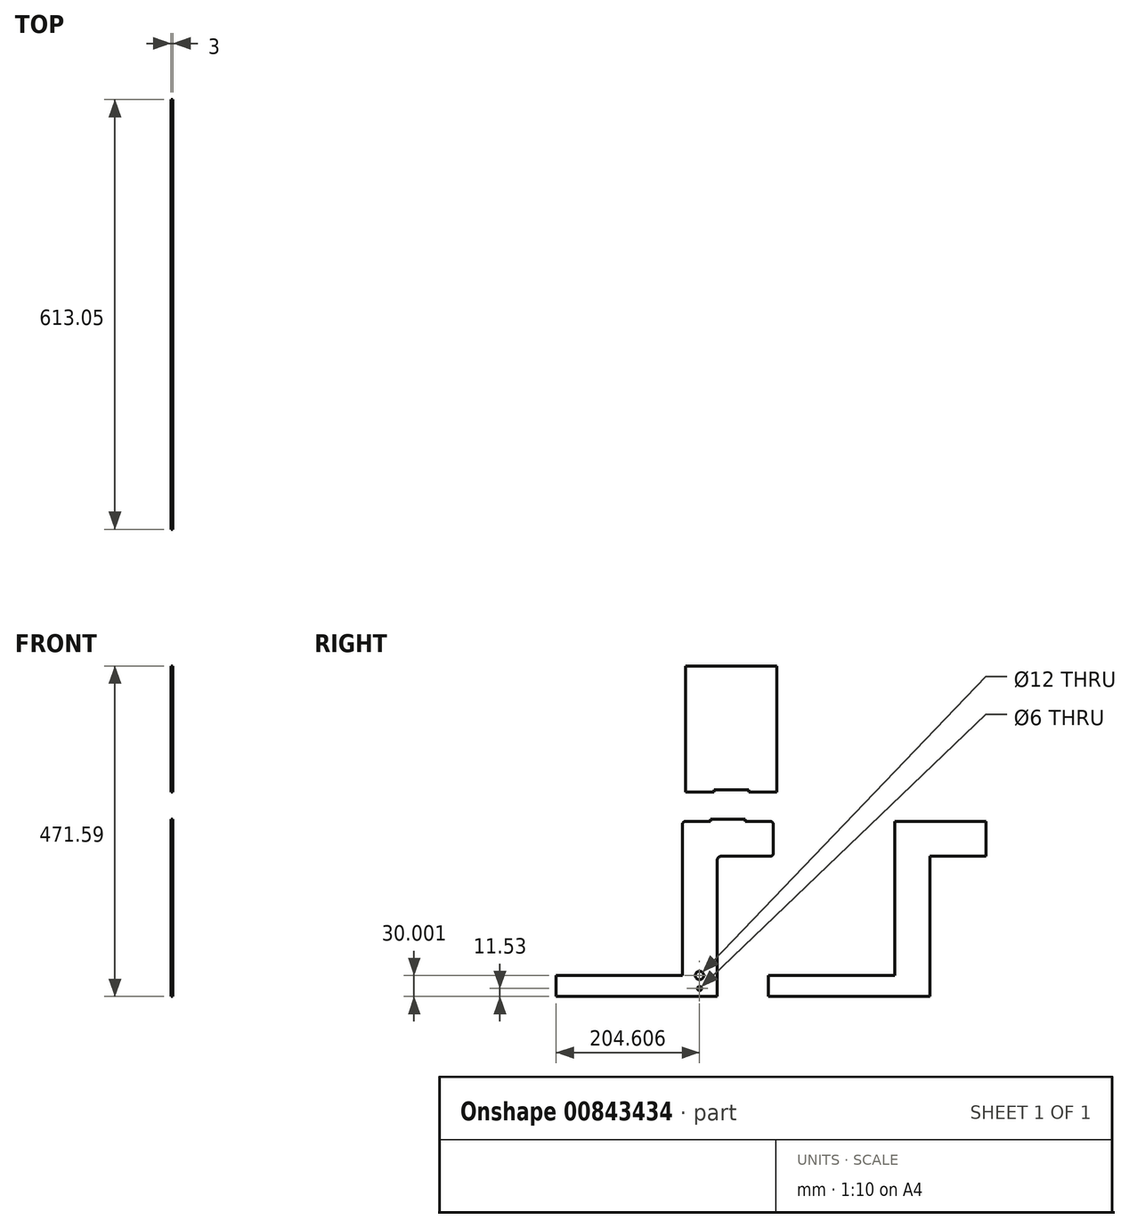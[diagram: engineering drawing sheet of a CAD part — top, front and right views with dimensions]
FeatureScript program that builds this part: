
annotation { "Feature Type Name" : "Feature", "Feature Type Description" : "" }
export const myFeature = defineFeature(function(context is Context, id is Id, definition is map)
    precondition{}
    {
        {
            var Q0;
            Q0=qCreatedBy(makeId("Right.planeOp"),FACE);
            var sketch = newSketch(context, id + "F0", { "sketchPlane" : qUnion([Q0])});
            skLineSegment(sketch, "E0", {"start": v(0, 42.16) * mm, "end": v(130, 42.16) * mm});
            skLineSegment(sketch, "E1", {"start": v(130, 42.16) * mm, "end": v(130, -7.84) * mm});
            skLineSegment(sketch, "E2", {"start": v(50, -7.84) * mm, "end": v(130, -7.84) * mm});
            skLineSegment(sketch, "E3", {"start": v(50, -7.84) * mm, "end": v(50, -207.84) * mm});
            skLineSegment(sketch, "E4", {"start": v(50, -207.84) * mm, "end": v(-180, -207.84) * mm});
            skLineSegment(sketch, "E5", {"start": v(-180, -207.84) * mm, "end": v(-180, -177.84) * mm});
            skLineSegment(sketch, "E6", {"start": v(0, -177.84) * mm, "end": v(-180, -177.84) * mm});
            skLineSegment(sketch, "E7", {"start": v(0, -177.84) * mm, "end": v(0, 42.16) * mm});
            skLineSegment(sketch, "E8", {"start": v(-298.05, 42.16) * mm, "end": v(-263.05, 42.16) * mm});
            skLineSegment(sketch, "E9", {"start": v(-173.05, 37.16) * mm, "end": v(-173.05, -2.84) * mm});
            skLineSegment(sketch, "E10", {"start": v(-248.05, -7.84) * mm, "end": v(-178.05, -7.84) * mm});
            skLineSegment(sketch, "E11", {"start": v(-253.05, -12.84) * mm, "end": v(-253.05, -207.84) * mm});
            skLineSegment(sketch, "E12", {"start": v(-253.05, -207.84) * mm, "end": v(-483.05, -207.84) * mm});
            skLineSegment(sketch, "E13", {"start": v(-483.05, -207.84) * mm, "end": v(-483.05, -177.84) * mm});
            skLineSegment(sketch, "E14", {"start": v(-303.05, -177.84) * mm, "end": v(-483.05, -177.84) * mm});
            skLineSegment(sketch, "E15", {"start": v(-303.05, -177.84) * mm, "end": v(-303.05, 37.16) * mm});
            skCircle(sketch, "E16", {"center": v(-278.44, -177.84) * mm, "radius": 6 * mm});
            skLineSegment(sketch, "E17.bottom", {"start": v(-298.36, 83.75) * mm, "end": v(-258.01, 83.75) * mm});
            skLineSegment(sketch, "E17.top", {"start": v(-298.36, 263.75) * mm, "end": v(-168.36, 263.75) * mm});
            skLineSegment(sketch, "E17.left", {"start": v(-298.36, 83.75) * mm, "end": v(-298.36, 263.75) * mm});
            skLineSegment(sketch, "E17.right", {"start": v(-168.36, 83.75) * mm, "end": v(-168.36, 263.75) * mm});
            skCircle(sketch, "E18", {"center": v(-278.44, -196.31) * mm, "radius": 3 * mm});
            skLineSegment(sketch, "E19", {"start": v(-263.05, 42.16) * mm, "end": v(-263.05, 45.16) * mm});
            skLineSegment(sketch, "E20", {"start": v(-263.05, 45.16) * mm, "end": v(-213.05, 45.16) * mm});
            skLineSegment(sketch, "E21", {"start": v(-213.05, 45.16) * mm, "end": v(-213.05, 42.16) * mm});
            skLineSegment(sketch, "E22.trimOffspring", {"start": v(-213.05, 42.16) * mm, "end": v(-178.05, 42.16) * mm});
            skLineSegment(sketch, "E23.top", {"start": v(-258.01, 86.75) * mm, "end": v(-208.01, 86.75) * mm});
            skLineSegment(sketch, "E23.left", {"start": v(-258.01, 83.75) * mm, "end": v(-258.01, 86.75) * mm});
            skLineSegment(sketch, "E23.right", {"start": v(-208.01, 83.75) * mm, "end": v(-208.01, 86.75) * mm});
            skLineSegment(sketch, "E24.trimOffspring", {"start": v(-208.01, 83.75) * mm, "end": v(-168.36, 83.75) * mm});
            skPoint(sketch, "E25.visualSharp", {"position": v(-303.05, 42.16) * mm});
            skArc(sketch, "E25.filletArc", {"start": v(-298.05, 42.16) * mm, "mid": v(-301.59, 40.7) * mm, "end": v(-303.05, 37.16) * mm});
            skPoint(sketch, "E26.visualSharp", {"position": v(-173.05, 42.16) * mm});
            skArc(sketch, "E26.filletArc", {"start": v(-173.05, 37.16) * mm, "mid": v(-174.52, 40.7) * mm, "end": v(-178.05, 42.16) * mm});
            skPoint(sketch, "E27.visualSharp", {"position": v(-173.05, -7.84) * mm});
            skArc(sketch, "E27.filletArc", {"start": v(-178.05, -7.84) * mm, "mid": v(-174.52, -6.37) * mm, "end": v(-173.05, -2.84) * mm});
            skPoint(sketch, "E28.visualSharp", {"position": v(-253.05, -7.84) * mm});
            skArc(sketch, "E28.filletArc", {"start": v(-248.05, -7.84) * mm, "mid": v(-251.59, -9.3) * mm, "end": v(-253.05, -12.84) * mm});
            skSolve(sketch);
        }
        {
            var Q0;
            Q0=makeQuery(id+"F0.imprint","IMPRINT",FACE,{"disambiguationData":[TD([[makeQuery(id+"F0.imprint","IMPRINT",EDGE,{"derivedFrom":sQuery(id+"F0.wireOp",EDGE,"E0")}),-1.0]])]});
            var Q1;
            Q1=makeQuery(id+"F0.imprint","IMPRINT",FACE,{"disambiguationData":[TD([[makeQuery(id+"F0.imprint","IMPRINT",EDGE,{"derivedFrom":sQuery(id+"F0.wireOp",EDGE,"E8")}),-1.0]])]});
            var Q2;
            Q2=makeQuery(id+"F0.imprint","IMPRINT",FACE,{"disambiguationData":[TD([[makeQuery(id+"F0.imprint","IMPRINT",EDGE,{"derivedFrom":sQuery(id+"F0.wireOp",EDGE,"E17.bottom")}),1.0]])]});
            extrude(context, id + "F1", {"entities" : qUnion([Q0, Q1, Q2]), "oppositeDirection" : true, "depth" : 3 * mm, "offsetDistance" : 25 * mm});
        }
    });
